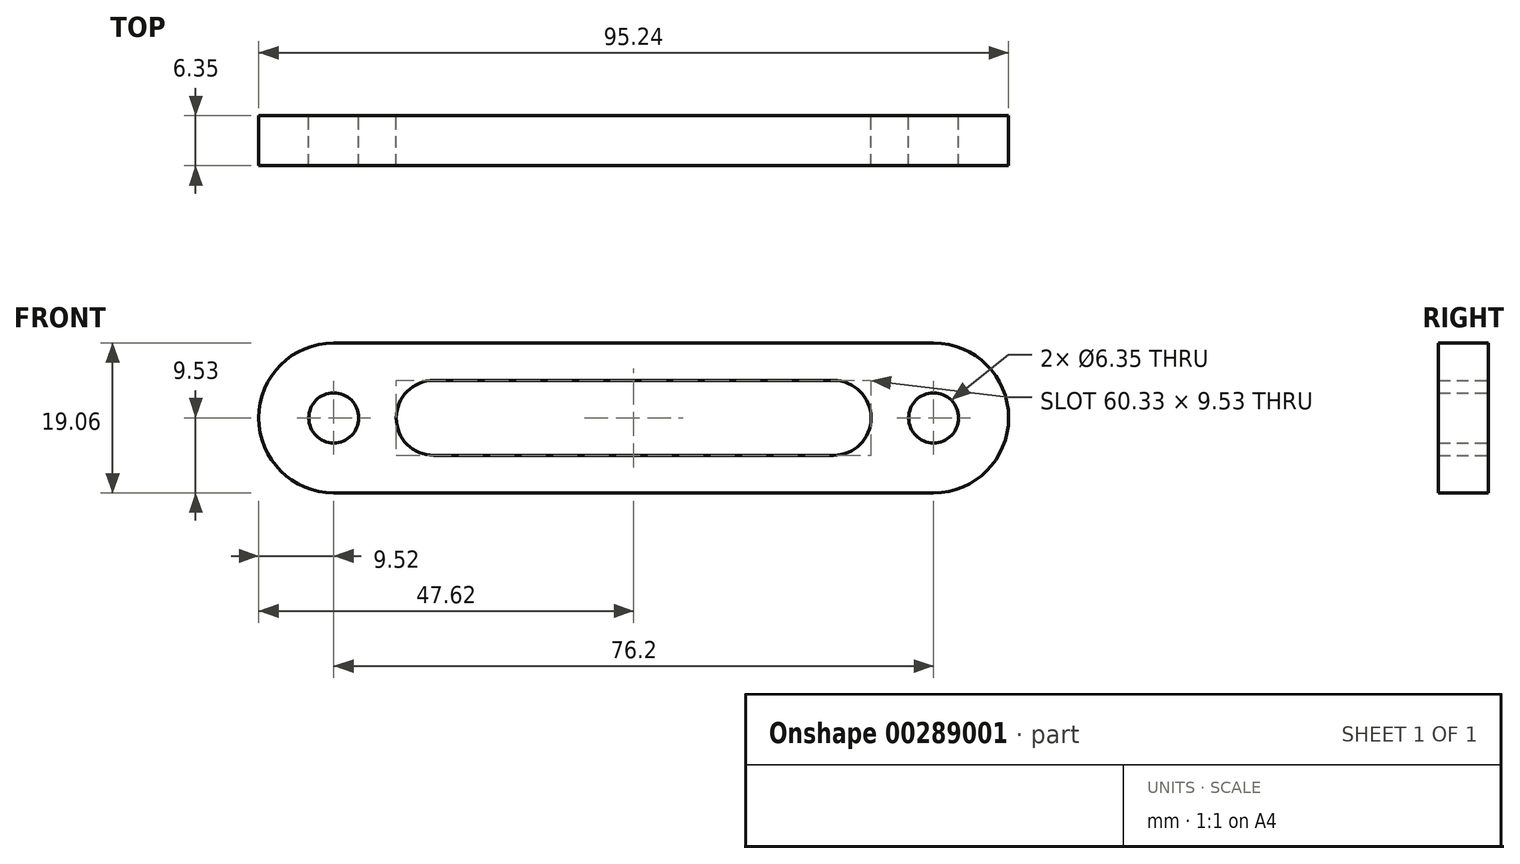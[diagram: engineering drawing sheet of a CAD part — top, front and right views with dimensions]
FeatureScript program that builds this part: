
annotation { "Feature Type Name" : "Feature", "Feature Type Description" : "" }
export const myFeature = defineFeature(function(context is Context, id is Id, definition is map)
    precondition{}
    {
        {
            var Q0;
            Q0=qCreatedBy(makeId("Front.planeOp"),FACE);
            var sketch = newSketch(context, id + "F0", { "sketchPlane" : qUnion([Q0])});
            skLineSegment(sketch, "E0.bottom", {"start": v(-38.1, 9.52) * mm, "end": v(38.1, 9.52) * mm});
            skLineSegment(sketch, "E0.top", {"start": v(-38.1, -9.52) * mm, "end": v(38.1, -9.52) * mm});
            skPoint(sketch, "E0.middle", {"position": v(0, 0) * mm});
            skCircle(sketch, "E1", {"center": v(-38.1, 0) * mm, "radius": 3.18 * mm});
            skCircle(sketch, "E2", {"center": v(38.1, 0) * mm, "radius": 3.18 * mm});
            skPoint(sketch, "E3.start.orphan", {"position": v(-12.7, 4.76) * mm});
            skPoint(sketch, "E4.start.orphan", {"position": v(-12.7, -4.76) * mm});
            skPoint(sketch, "E5.center.orphan", {"position": v(-12.7, 0) * mm});
            skArc(sketch, "E6", {"start": v(-25.4, 4.76) * mm, "mid": v(-30.16, 0) * mm, "end": v(-25.4, -4.76) * mm});
            skLineSegment(sketch, "E7", {"start": v(-25.4, 4.76) * mm, "end": v(25.4, 4.76) * mm});
            skLineSegment(sketch, "E8", {"start": v(-25.4, -4.76) * mm, "end": v(25.4, -4.76) * mm});
            skArc(sketch, "E9", {"start": v(25.4, -4.76) * mm, "mid": v(30.16, 0) * mm, "end": v(25.4, 4.76) * mm});
            skArc(sketch, "E10", {"start": v(-38.1, 9.52) * mm, "mid": v(-47.62, 0) * mm, "end": v(-38.1, -9.52) * mm});
            skArc(sketch, "E11", {"start": v(38.1, -9.52) * mm, "mid": v(47.62, 0) * mm, "end": v(38.1, 9.52) * mm});
            skSolve(sketch);
        }
        {
            var Q0;
            Q0=makeQuery(id+"F0.imprint","IMPRINT",FACE,{"disambiguationData":[TD([[makeQuery(id+"F0.imprint","IMPRINT",EDGE,{"derivedFrom":sQuery(id+"F0.wireOp",EDGE,"E0.bottom")}),-1.0]])]});
            extrude(context, id + "F1", {"entities" : qUnion([Q0]), "depth" : 6.35 * mm});
        }
    });
